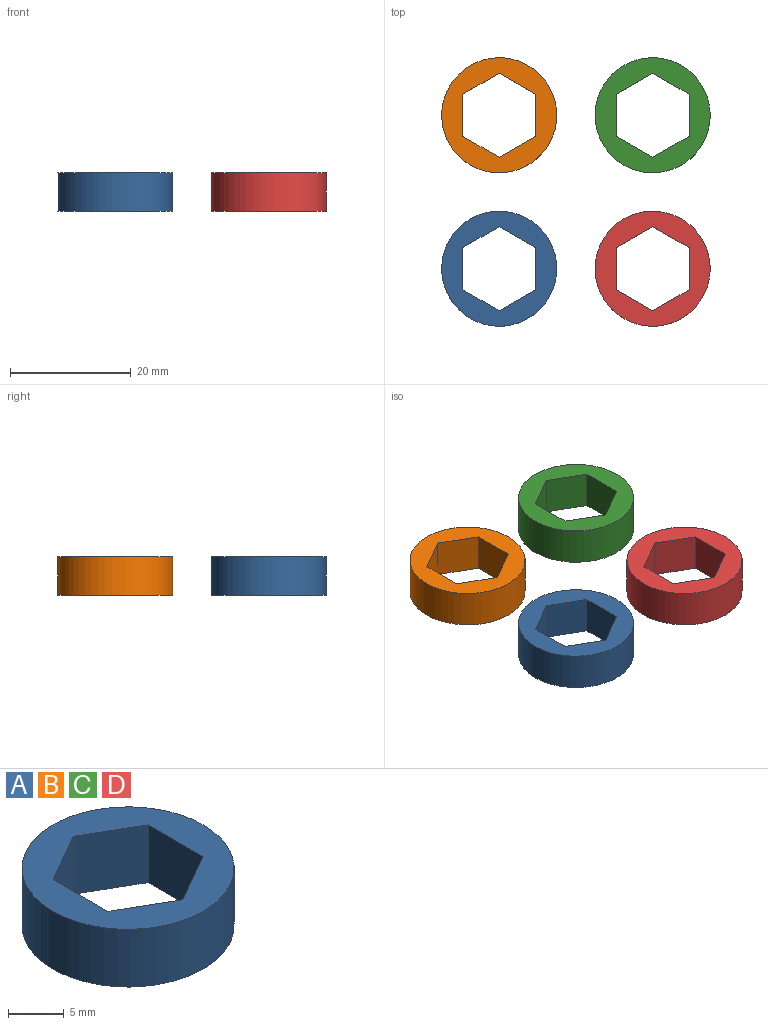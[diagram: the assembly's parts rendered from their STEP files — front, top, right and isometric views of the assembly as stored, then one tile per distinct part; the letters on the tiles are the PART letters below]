
ASSEMBLY  parts=4 mates=3
PART A: 9 faces, bbox 19.1x19.1x6.4 mm
  f0: plane 6.35x6.03mm, normal (-0.5,-0.87,0), area 44.2mm2, adj f1,f6,f7,f8
  f1: plane 6.97x6.35mm, normal (-1,0,0), area 44.2mm2, adj f0,f2,f7,f8
  f2: plane 6.35x6.03mm, normal (-0.5,0.87,0), area 44.2mm2, adj f1,f3,f7,f8
  f3: plane 6.35x6.03mm, normal (0.5,0.87,0), area 44.2mm2, adj f2,f4,f7,f8
  f4: plane 6.97x6.35mm, normal (1,0,0), area 44.2mm2, adj f3,f6,f7,f8
  f5: cylinder r=9.53mm len=19.05mm, axis (0,0,-1), area 380mm2, adj f7,f8
  f6: plane 6.35x6.03mm, normal (0.5,-0.87,0), area 44.2mm2, adj f0,f4,f7,f8
  f7: plane 19.05x19.05mm, normal (0,0,1), area 159mm2, adj f0,f1,f2,f3,f4,f5,f6
  f8: plane 19.05x19.05mm, normal (0,0,-1), area 159mm2, adj f0,f1,f2,f3,f4,f5,f6
PART B: same geometry as A
PART C: same geometry as A
PART D: same geometry as A
PLACE A t=(-22.08,-27.19,-1.43)mm
PLACE B t=(-22.08,-1.79,-1.43)mm
PLACE C t=(3.32,-1.79,-1.43)mm
PLACE D t=(3.32,-27.19,-1.43)mm
MATE fastened A.f5 <-> B.f8  axis (0,0,-1) through (-22.08,-27.19,-1.43)mm
MATE fastened D.f5 <-> C.f8  axis (0,0,-1) through (3.32,-27.19,-1.43)mm
MATE fastened D.f5 <-> A.f8  axis (0,0,-1) through (3.32,-27.19,-1.43)mm
